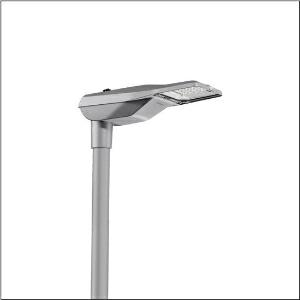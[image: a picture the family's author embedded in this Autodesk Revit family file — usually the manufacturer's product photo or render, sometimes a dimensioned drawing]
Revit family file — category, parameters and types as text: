
# Revit family: streetlight_sl_21_micro___stw1_0a_5xe1e33s08db_cbec
name_source: partatom
category: Lighting Fixtures
units: mm (PartAtom-declared; Revit-internal decimal feet)

## family parameters
Cut with Voids When Loaded = No
Host = Face
Light Source = No
Part Type = Normal
Room Calculation Point = No
Round Connector Dimension = Use Diameter
Shared = No

## types (1)
- --- (1 x LED, 5110 lm, 39.1 W, 3000K)
    Apparent Load = 39 VA
    CIE Flux Codes = 38 75 98 100 100
    Color Rendering = 70
    Color Temperature = 3000K
    Default Elevation = 1800 mm
    Description = Streetlight SL 21 micro, mast luminaire, primary light control with lens, of PMMA, primary optical cover: cover, of toughened safety glass, transparent, light distribution: STW1.0a, light emission: direct distribution, primary light characteristic: asymmetric, installation type: side-entry, post-top, LED, High Power LED, rated luminous flux: 5.110lm, luminous efficacy: 131lm/W, light colour: 730, colour temperature: 3000K, control: flexible luminous flux parameterisation, time-dependent luminous flux control, constant luminous flux control, overheat protection, presetting dimming logarithmic, mains connection: 220..240V, AC, 50/60Hz, start of lifetime: 39W, end of service life: 41W, reduction: 18W, luminaire housing, of diecast aluminium, powder-coated, Siteco® metallic grey (DB 702S), corrosivity category C5 mid according to DIN EN ISO 12944, please order mast flange separately, inclination adjustable: 0°, 5°, 10°, 15°, sealing non-destructively replaceable, multi-level sealing system, length: 528mm, width: 235mm, height: 110mm, mast flange for spigot size: 42mm (side-entry): 5XC10008XM4, 60/48mm (side-entry/post-top): 5XC10108XM2, 76/60mm (side-entry/post-top): 5XC10108XM1, Smart Interface above, protection rating (complete): IP66, insulation class (complete): insulation class II (safety insulation), certification: CE, ENEC, ENEC+, VDE, impact resistance: IK09, permissible operating ambient temperature for outdoor applications: -40..+50°C, standard-compliant lighting for roads and squares, packaging unit: 1 piece

Light Distribution: STW1.0a
    Height = 110 mm
    Lamp = 1 x LED
    Lamp Light Flux = 5110 lm
    Lamp Power = 39.1 W
    Lamp count = 1
    Length = 528 mm
    Luminous efficacy = 131 lm/W
    Manufacturer = Siteco
    ModVariant = No
    Model = 5XE1E33S08DB
    Number of Poles = 1
    OnlyDefault = Yes
    Power Factor = 1
    Product Name = Streetlight SL 21 micro | STW1.0a
    Product group = mast luminaire | pylon top
    ProductGroupID = 6100
    Protection Class = Protection class II
    Protection Degree = IP 66
    RLX_Detail_Level = 1
    RLX_Emergency_Light_Flux = 0 lm
    RLX_Emergency_Type = 0
    RLX_Emergency_Type_DB = No
    RlxData = <blob elided: 99217 chars, md5=dd54b07e>
    Socket = socket
    Standby Power = 0 W
    System Light Flux = 5110 lm
    System Power = 39 W
    Type Comments = factory setting: luminous flux: 100 % | dim-lin: 254 | 765 mA
    Type Image = l_1277292.jpg
    URL = http://relux.com
    VarID = @adj_105503
    Voltage = 0 V
    Weight = 0.00 kg
    Width = 235 mm

## geometry (parser evidence)
native form markers: Blend x4, Sweep x10
no freeform markers — native parametric forms only
